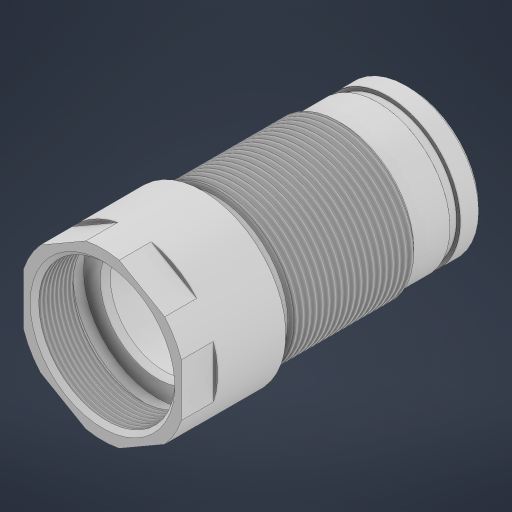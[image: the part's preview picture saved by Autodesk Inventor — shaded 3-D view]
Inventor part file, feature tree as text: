
AUTODESK INVENTOR PART (.ipt)
format: ipt  version: 2024.3 (Build 283343000, 343)  size: 369,664 bytes
history: native  units: mm
features: thread x2, sketch x2, revolve x1, extrude x1
ambient origin geometry x8: Origin, YZ Plane, XZ Plane, XY Plane, X Axis, Y Axis, Z Axis, Center Point
bodies: Solid1 (feature_tree)
feature tree (6):
  revolve  "Revolution1"  [1 undecoded]
  thread  "Thread1"  [1 undecoded]
  thread  "Thread2"  [1 undecoded]
  extrude  "Extrusion1"  TaperAngle=90.0deg  [1 undecoded]
  sketch  "Sketch1"  dims[d2=32.0mm d4=2.0mm d8=65.0mm d12=5.0mm]
  sketch  "Sketch2"  dims[d14=32.0mm d16=90.0deg d18=90.0deg d22=90.0deg d23=4.0mm d24=45.0deg d25=5.0mm d26=135.0deg d28=120.0deg d30=6.0mm d31=60.0deg d32=150.0deg d33=1.6mm d34=1.6mm d35=1.6mm d36=1.6mm d37=2.0mm d38=2.0mm d39=4.7mm d41=90.0deg d42=0.1mm d43=90.0deg d44=56.172mm d45=0.0mm d46=16.042mm d47=0.0mm d48=74.0mm d49=47.0mm d50=0.0mm d51=0.5mm d52=0.872665mm d53=0.5mm d54=0.872665mm]
note: 4 required parameter values undecoded (feature->parameter linkage not recoverable at this tier; creation-order binding heuristic only, values carry confidence <= 0.55)